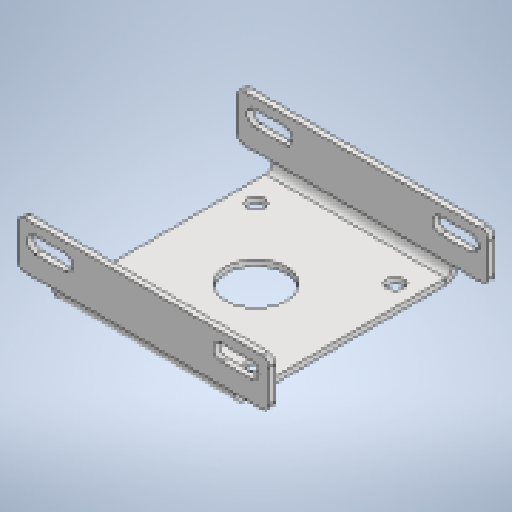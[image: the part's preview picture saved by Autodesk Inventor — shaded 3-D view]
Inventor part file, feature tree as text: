
AUTODESK INVENTOR PART (.ipt)
format: ipt  version: 2025.1 (Build 291241020, 241B)  size: 314,880 bytes
history: native  units: mm
features: sheet_metal_op x4, sketch x4, other x4, extrude x1, mirror x1, chamfer x1, projected_geometry x1
ambient origin geometry x8: Origin, YZ Plane, XZ Plane, XY Plane, X Axis, Y Axis, Z Axis, Center Point
bodies: Solid1 (feature_tree)
feature tree (16):
  sheet_metal_op  "Face1"
  sheet_metal_op  "Flange2"
  extrude  "Extrusion4"  Depth=5.0mm
  mirror  "Mirror1"
  chamfer  "Corner Round1"
  sketch  "Sketch1"  dims[d2=5.0mm d25=150.0mm]
  other  "Plate1"
  sketch  "Sketch5"  dims[d26=166.0mm]
  other  "Plate3"
  sheet_metal_op  "Bend2"
  sheet_metal_op  "Corner2"
  sketch  "Sketch6"  dims[d27=5.0mm]
  sketch  "Sketch10"  dims[d28=2.5mm d29=10.0mm d30=6.0mm d31=50.0mm d32=90.0deg d33=6.0mm d34=20.0mm d35=1.0mm d36=6.0mm d39=5.0mm d40=0.0mm d55=14.0mm d56=116.0mm d57=116.0mm d60=50.0mm d61=210.0mm d62=13.0mm d63=25.0mm d64=15.0mm d65=15.0mm d66=0.0mm d67=0.0mm d68=6.0mm]
  projected_geometry  "Projected Loop3"
  other  "Cut1"
  other  "Definition1"
